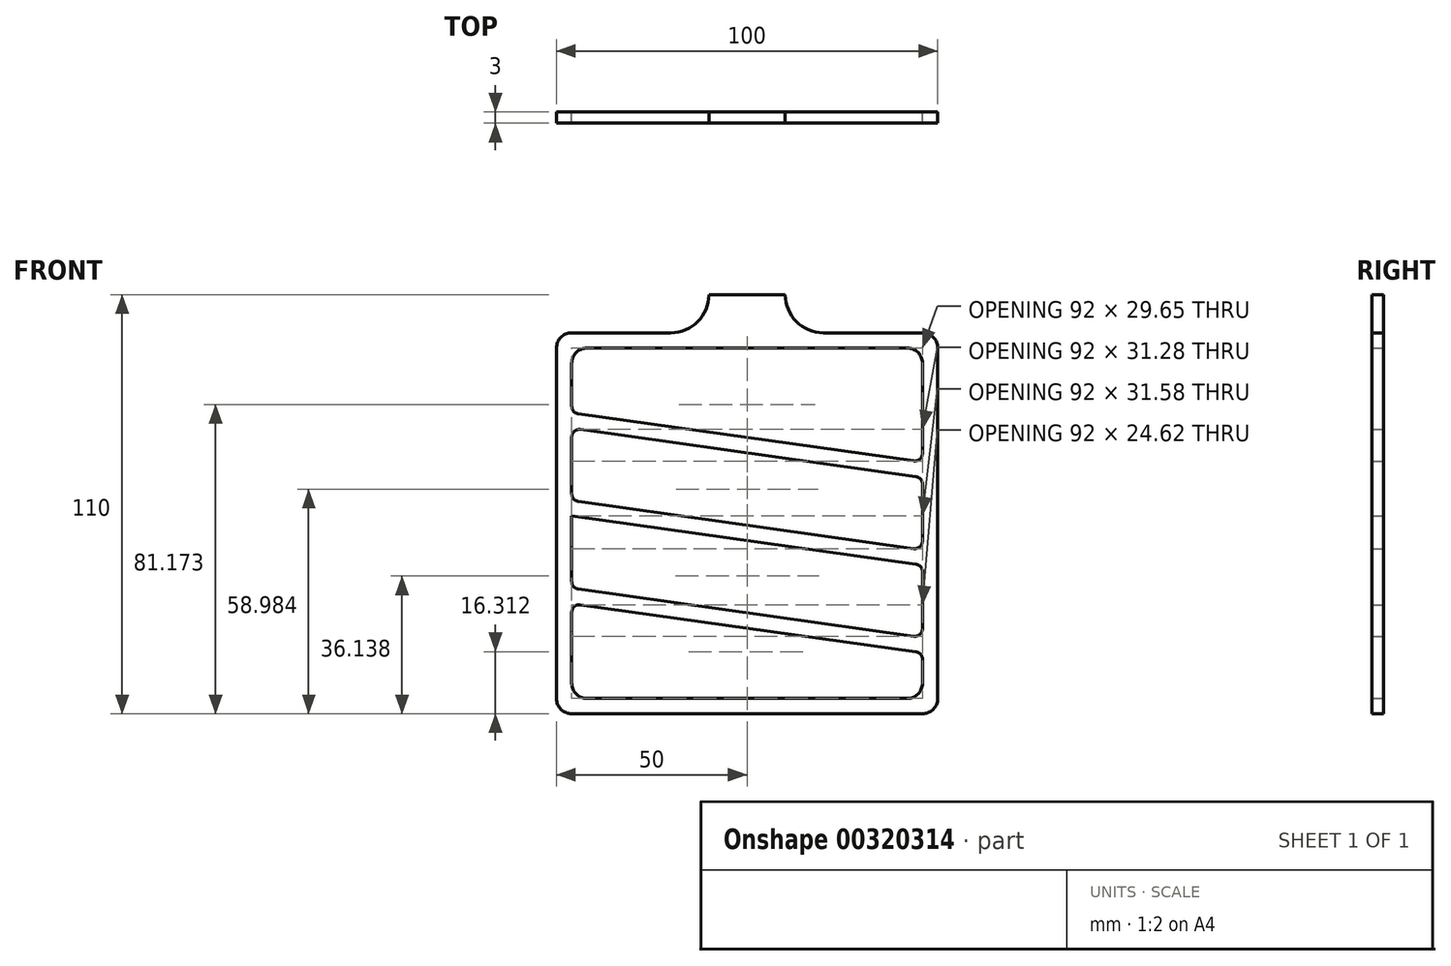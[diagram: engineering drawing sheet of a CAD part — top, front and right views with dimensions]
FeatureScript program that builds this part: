
annotation { "Feature Type Name" : "Feature", "Feature Type Description" : "" }
export const myFeature = defineFeature(function(context is Context, id is Id, definition is map)
    precondition{}
    {
        {
            var Q0;
            Q0=qCreatedBy(makeId("Front.planeOp"),FACE);
            var sketch = newSketch(context, id + "F0", { "sketchPlane" : qUnion([Q0])});
            skLineSegment(sketch, "E0.bottom", {"start": v(4, 0) * mm, "end": v(96, 0) * mm});
            skLineSegment(sketch, "E0.top", {"start": v(70, 100) * mm, "end": v(96, 100) * mm});
            skLineSegment(sketch, "E0.left", {"start": v(0, 4) * mm, "end": v(0, 96) * mm});
            skLineSegment(sketch, "E0.right", {"start": v(100, 4) * mm, "end": v(100, 96) * mm});
            skLineSegment(sketch, "E1.0", {"start": v(8, 96) * mm, "end": v(92, 96) * mm});
            skLineSegment(sketch, "E1.1", {"start": v(4, 80.7) * mm, "end": v(4, 92) * mm});
            skLineSegment(sketch, "E1.2", {"start": v(8, 4) * mm, "end": v(92, 4) * mm});
            skLineSegment(sketch, "E1.3", {"start": v(96, 68.34) * mm, "end": v(96, 92) * mm});
            skLineSegment(sketch, "E2", {"start": v(6.28, 28.6) * mm, "end": v(94.28, 16.24) * mm});
            skLineSegment(sketch, "E3.0", {"start": v(5.72, 32.73) * mm, "end": v(93.72, 20.36) * mm});
            skLineSegment(sketch, "E4.0.1.0", {"start": v(4, 51.93) * mm, "end": v(94.28, 39.24) * mm});
            skLineSegment(sketch, "E4.0.1.1", {"start": v(5.72, 55.73) * mm, "end": v(93.72, 43.36) * mm});
            skLineSegment(sketch, "E4.0.2.0", {"start": v(6.28, 74.6) * mm, "end": v(94.28, 62.24) * mm});
            skLineSegment(sketch, "E4.0.2.1", {"start": v(5.72, 78.73) * mm, "end": v(93.72, 66.36) * mm});
            skLineSegment(sketch, "E4.direction1", {"start": v(4, 28.93) * mm, "end": v(29, 28.93) * mm, "construction": true});
            skLineSegment(sketch, "E4.direction2", {"start": v(4, 28.93) * mm, "end": v(4, 51.93) * mm, "construction": true});
            skLineSegment(sketch, "E5.bottom", {"start": v(40, 100) * mm, "end": v(60, 100) * mm});
            skPoint(sketch, "E5.middle", {"position": v(50, 114.5) * mm});
            skLineSegment(sketch, "E6.bottom", {"start": v(45.05, 100) * mm, "end": v(54.95, 100) * mm});
            skLineSegment(sketch, "E6.left", {"start": v(45.05, 111) * mm, "end": v(45.05, 114.5) * mm});
            skLineSegment(sketch, "E6.right", {"start": v(54.95, 111) * mm, "end": v(54.95, 114.5) * mm});
            skLineSegment(sketch, "E7", {"start": v(47.45, 111) * mm, "end": v(54.95, 111) * mm});
            skLineSegment(sketch, "E8", {"start": v(47.45, 111) * mm, "end": v(45.05, 111) * mm});
            skLineSegment(sketch, "E9", {"start": v(43, 114.5) * mm, "end": v(45.05, 114.5) * mm});
            skLineSegment(sketch, "E10.trimOffspring", {"start": v(54.95, 114.5) * mm, "end": v(57, 114.5) * mm});
            skPoint(sketch, "E11.start.orphan", {"position": v(50, 100) * mm});
            skPoint(sketch, "E12.visualSharp", {"position": v(40, 114.5) * mm});
            skPoint(sketch, "E13.visualSharp", {"position": v(60, 114.5) * mm});
            skPoint(sketch, "E14.newPointA", {"position": v(0, 100) * mm});
            skPoint(sketch, "E14.newPointB", {"position": v(60, 100) * mm});
            skArc(sketch, "E14.filletArc", {"start": v(60, 110) * mm, "mid": v(62.93, 102.93) * mm, "end": v(70, 100) * mm});
            skLineSegment(sketch, "E15", {"start": v(30, 100) * mm, "end": v(4, 100) * mm});
            skPoint(sketch, "E16.visualSharp", {"position": v(40, 100) * mm});
            skArc(sketch, "E16.filletArc", {"start": v(30, 100) * mm, "mid": v(37.07, 102.93) * mm, "end": v(40, 110) * mm});
            skArc(sketch, "E17.filletArc", {"start": v(4, 100) * mm, "mid": v(1.17, 98.83) * mm, "end": v(0, 96) * mm});
            skArc(sketch, "E18.filletArc", {"start": v(8, 96) * mm, "mid": v(5.17, 94.83) * mm, "end": v(4, 92) * mm});
            skPoint(sketch, "E19.visualSharp", {"position": v(96, 96) * mm});
            skArc(sketch, "E19.filletArc", {"start": v(96, 92) * mm, "mid": v(94.83, 94.83) * mm, "end": v(92, 96) * mm});
            skPoint(sketch, "E20.visualSharp", {"position": v(100, 100) * mm});
            skArc(sketch, "E20.filletArc", {"start": v(100, 96) * mm, "mid": v(98.83, 98.83) * mm, "end": v(96, 100) * mm});
            skPoint(sketch, "E21.visualSharp", {"position": v(96, 4) * mm});
            skArc(sketch, "E21.filletArc", {"start": v(92, 4) * mm, "mid": v(94.83, 5.17) * mm, "end": v(96, 8) * mm});
            skPoint(sketch, "E22.visualSharp", {"position": v(100, 0) * mm});
            skArc(sketch, "E22.filletArc", {"start": v(96, 0) * mm, "mid": v(98.83, 1.17) * mm, "end": v(100, 4) * mm});
            skPoint(sketch, "E23.visualSharp", {"position": v(0, 0) * mm});
            skArc(sketch, "E23.filletArc", {"start": v(0, 4) * mm, "mid": v(1.17, 1.17) * mm, "end": v(4, 0) * mm});
            skArc(sketch, "E24.filletArc", {"start": v(4, 8) * mm, "mid": v(5.17, 5.17) * mm, "end": v(8, 4) * mm});
            skPoint(sketch, "E25.newPointA", {"position": v(4, 78.97) * mm});
            skArc(sketch, "E25.filletArc", {"start": v(4, 80.7) * mm, "mid": v(4.5, 79.4) * mm, "end": v(5.72, 78.73) * mm});
            skPoint(sketch, "E26.newPointA", {"position": v(96, 66.04) * mm});
            skArc(sketch, "E26.filletArc", {"start": v(93.72, 66.36) * mm, "mid": v(95.31, 66.83) * mm, "end": v(96, 68.34) * mm});
            skLineSegment(sketch, "E27", {"start": v(4, 72.63) * mm, "end": v(4, 57.7) * mm});
            skLineSegment(sketch, "E28", {"start": v(4, 51.93) * mm, "end": v(4, 34.7) * mm});
            skLineSegment(sketch, "E29", {"start": v(4, 26.63) * mm, "end": v(4, 8) * mm});
            skLineSegment(sketch, "E30", {"start": v(96, 8) * mm, "end": v(96, 14.26) * mm});
            skLineSegment(sketch, "E31", {"start": v(96, 22.34) * mm, "end": v(96, 37.26) * mm});
            skLineSegment(sketch, "E32", {"start": v(96, 45.34) * mm, "end": v(96, 60.26) * mm});
            skPoint(sketch, "E33.visualSharp", {"position": v(4, 74.93) * mm});
            skArc(sketch, "E33.filletArc", {"start": v(6.28, 74.6) * mm, "mid": v(4.69, 74.14) * mm, "end": v(4, 72.63) * mm});
            skPoint(sketch, "E34.visualSharp", {"position": v(4, 55.97) * mm});
            skArc(sketch, "E34.filletArc", {"start": v(4, 57.7) * mm, "mid": v(4.5, 56.4) * mm, "end": v(5.72, 55.73) * mm});
            skPoint(sketch, "E35.visualSharp", {"position": v(96, 43.04) * mm});
            skArc(sketch, "E35.filletArc", {"start": v(93.72, 43.36) * mm, "mid": v(95.31, 43.83) * mm, "end": v(96, 45.34) * mm});
            skPoint(sketch, "E36.visualSharp", {"position": v(96, 62) * mm});
            skArc(sketch, "E36.filletArc", {"start": v(96, 60.26) * mm, "mid": v(95.5, 61.57) * mm, "end": v(94.28, 62.24) * mm});
            skPoint(sketch, "E37.visualSharp", {"position": v(96, 39) * mm});
            skArc(sketch, "E37.filletArc", {"start": v(96, 37.26) * mm, "mid": v(95.5, 38.57) * mm, "end": v(94.28, 39.24) * mm});
            skPoint(sketch, "E38.visualSharp", {"position": v(96, 20.04) * mm});
            skArc(sketch, "E38.filletArc", {"start": v(93.72, 20.36) * mm, "mid": v(95.31, 20.83) * mm, "end": v(96, 22.34) * mm});
            skPoint(sketch, "E39.visualSharp", {"position": v(4, 32.97) * mm});
            skArc(sketch, "E39.filletArc", {"start": v(4, 34.7) * mm, "mid": v(4.5, 33.4) * mm, "end": v(5.72, 32.73) * mm});
            skPoint(sketch, "E40.visualSharp", {"position": v(96, 16) * mm});
            skArc(sketch, "E40.filletArc", {"start": v(96, 14.26) * mm, "mid": v(95.5, 15.57) * mm, "end": v(94.28, 16.24) * mm});
            skPoint(sketch, "E41.visualSharp", {"position": v(4, 28.93) * mm});
            skArc(sketch, "E41.filletArc", {"start": v(6.28, 28.6) * mm, "mid": v(4.69, 28.14) * mm, "end": v(4, 26.63) * mm});
            skLineSegment(sketch, "E42.bottom", {"start": v(60, 110) * mm, "end": v(40, 110) * mm});
            skLineSegment(sketch, "E42.top", {"start": v(60, 120.74) * mm, "end": v(40, 120.74) * mm});
            skLineSegment(sketch, "E42.left", {"start": v(60, 110) * mm, "end": v(60, 120.74) * mm});
            skLineSegment(sketch, "E42.right", {"start": v(40, 110) * mm, "end": v(40, 120.74) * mm});
            skSolve(sketch);
        }
        {
            var Q0;
            Q0=makeQuery(id+"F0.imprint","IMPRINT",FACE,{"disambiguationData":[TD([[makeQuery(id+"F0.imprint","IMPRINT",EDGE,{"derivedFrom":sQuery(id+"F0.wireOp",EDGE,"E0.bottom")}),1.0]])]});
            extrude(context, id + "F1", {"entities" : qUnion([Q0]), "depth" : 3 * mm, "offsetDistance" : 25 * mm});
        }
    });
